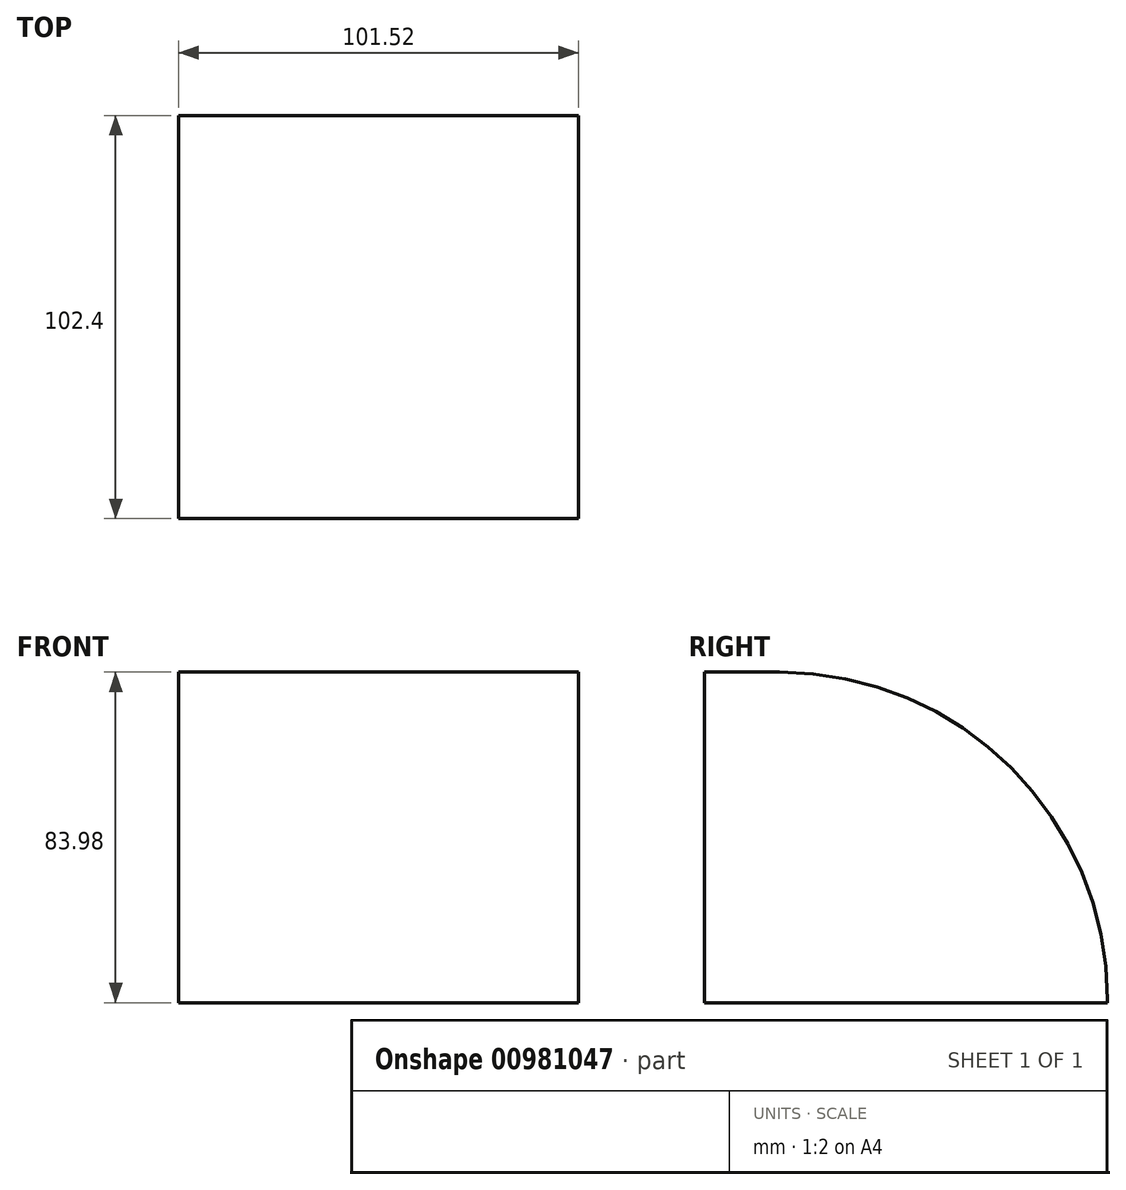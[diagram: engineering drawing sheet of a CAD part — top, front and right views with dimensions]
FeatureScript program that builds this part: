
annotation { "Feature Type Name" : "Feature", "Feature Type Description" : "" }
export const myFeature = defineFeature(function(context is Context, id is Id, definition is map)
    precondition{}
    {
        {
            var Q0;
            Q0=qCreatedBy(makeId("Front.planeOp"),FACE);
            var sketch = newSketch(context, id + "F0", { "sketchPlane" : qUnion([Q0])});
            skLineSegment(sketch, "E0.bottom", {"start": v(50.76, 41.99) * mm, "end": v(-50.76, 41.99) * mm});
            skLineSegment(sketch, "E0.top", {"start": v(50.76, -41.99) * mm, "end": v(-50.76, -41.99) * mm});
            skLineSegment(sketch, "E0.left", {"start": v(50.76, 41.99) * mm, "end": v(50.76, -41.99) * mm});
            skLineSegment(sketch, "E0.right", {"start": v(-50.76, 41.99) * mm, "end": v(-50.76, -41.99) * mm});
            skPoint(sketch, "E0.middle", {"position": v(0, 0) * mm});
            skSolve(sketch);
        }
        {
            var Q0;
            Q0=makeQuery(id+"F0.imprint","IMPRINT",FACE,{"disambiguationData":[TD([[makeQuery(id+"F0.imprint","IMPRINT",EDGE,{"derivedFrom":sQuery(id+"F0.wireOp",EDGE,"E0.bottom")}),1.0]])]});
            extrude(context, id + "F1", {"entities" : qUnion([Q0]), "oppositeDirection" : true, "depth" : 102.4 * mm, "offsetDistance" : 25 * mm});
        }
        {
            var Q0;
            Q0=makeQuery(id+"F1.opExtrude","CAP_EDGE",EDGE,{"disambiguationData":[OSD([sQuery(id+"F0.wireOp",EDGE,"E0.bottom")])],"isStart":false});
            fillet(context, id + "F2", {"entities" : qUnion([Q0]), "radius" : 83.3 * mm, "tangentPropagation" : true, "allowEdgeOverflow" : false});
        }
    });
